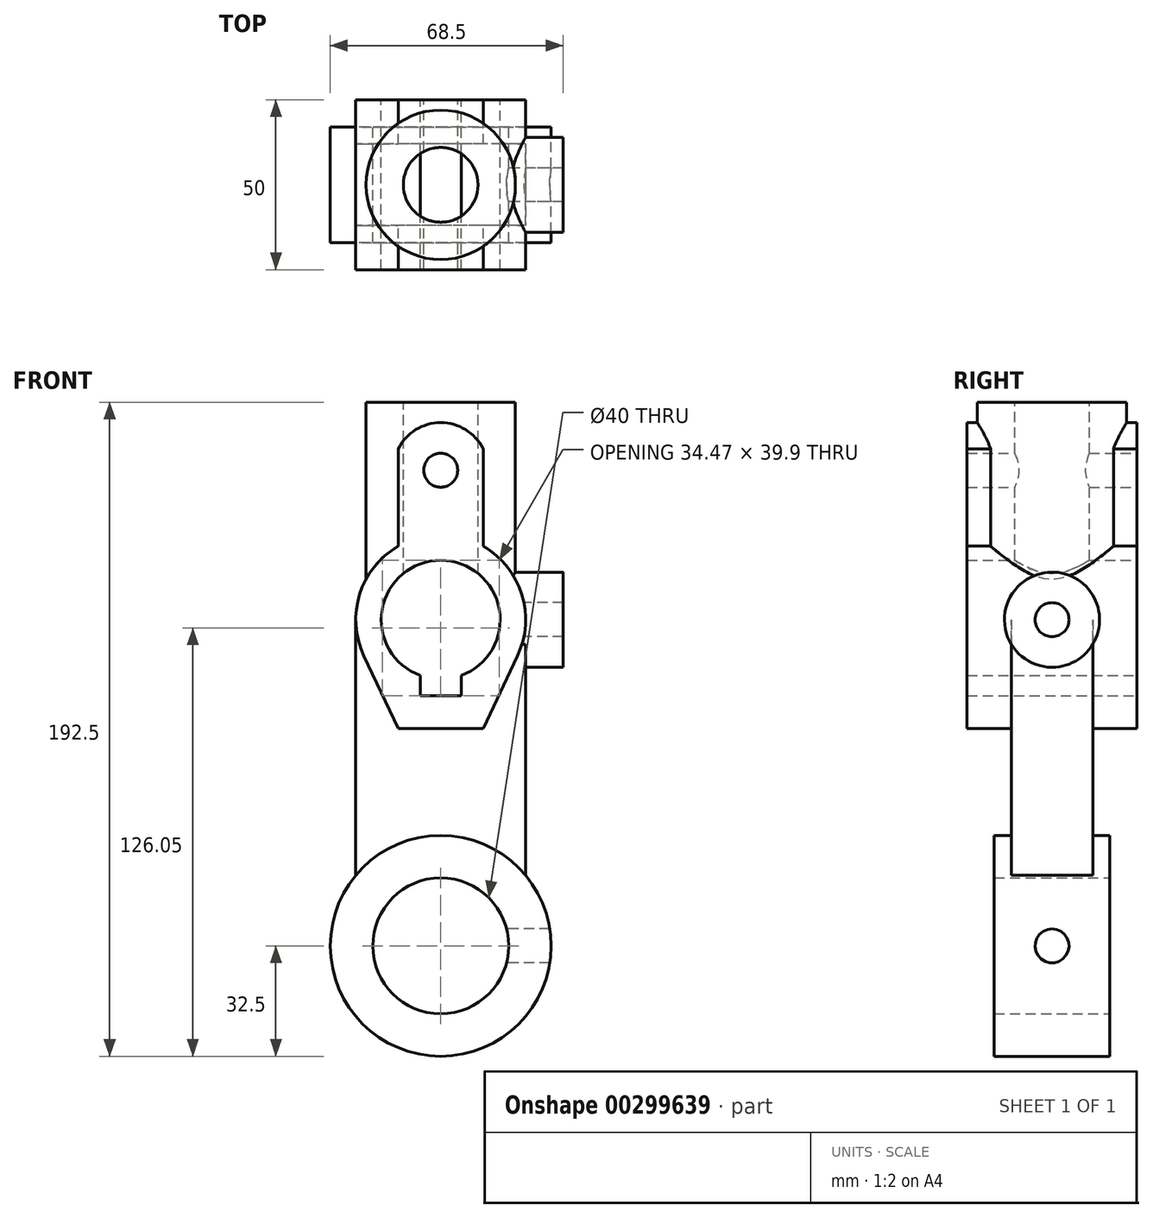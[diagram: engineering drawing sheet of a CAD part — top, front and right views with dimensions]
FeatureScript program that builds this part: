
annotation { "Feature Type Name" : "Feature", "Feature Type Description" : "" }
export const myFeature = defineFeature(function(context is Context, id is Id, definition is map)
    precondition{}
    {
        {
            var Q0;
            Q0=qCreatedBy(makeId("Front.planeOp"),FACE);
            var sketch = newSketch(context, id + "F0", { "sketchPlane" : qUnion([Q0])});
            skCircle(sketch, "E0", {"center": v(0, 0) * mm, "radius": 32.5 * mm});
            skCircle(sketch, "E1", {"center": v(0, 0) * mm, "radius": 20 * mm});
            skPoint(sketch, "E2.trimOffspring.end.orphan", {"position": v(25, 0) * mm});
            skPoint(sketch, "E3.left.start.orphan", {"position": v(-25, 0) * mm});
            skSolve(sketch);
        }
        {
            var Q0;
            Q0 = qSketchRegion(id + "F0", true);
            extrude(context, id + "F1", {"entities" : qUnion([Q0]), "endBound" : BoundingType.SYMMETRIC, "depth" : 34 * mm});
        }
        {
            var Q0;
            Q0=qCreatedBy(makeId("Front.planeOp"),FACE);
            var sketch = newSketch(context, id + "F2", { "sketchPlane" : qUnion([Q0])});
            skLineSegment(sketch, "E4", {"start": v(-25, 0) * mm, "end": v(25, 0) * mm});
            skLineSegment(sketch, "E5", {"start": v(25, 0) * mm, "end": v(25, 96) * mm});
            skLineSegment(sketch, "E6", {"start": v(-25, 0) * mm, "end": v(-25, 96) * mm});
            skLineSegment(sketch, "E7", {"start": v(-25, 96) * mm, "end": v(25, 96) * mm});
            skSolve(sketch);
        }
        {
            var Q0;
            Q0=makeQuery(id+"F2.imprint","IMPRINT",FACE,{"disambiguationData":[TD([[makeQuery(id+"F2.imprint","IMPRINT",EDGE,{"derivedFrom":sQuery(id+"F2.wireOp",EDGE,"E4")}),1.0]])]});
            extrude(context, id + "F3", {"entities" : qUnion([Q0]), "operationType" : NewBodyOperationType.ADD, "endBound" : BoundingType.SYMMETRIC, "depth" : 24 * mm});
        }
        {
            var Q0;
            {var subQ0=sQuery(id+"F2.wireOp",EDGE,"E4");Q0=makeQuery(id+"F3.boolean.opBoolean","SPLIT",FACE,{"disambiguationData":[TD([makeQuery(id+"F1.opExtrude","SWEPT_FACE",FACE,{"disambiguationData":[OSD([sQuery(id+"F0.wireOp",EDGE,"E1")])]})])],"derivedFrom":makeQuery(id+"F3.opExtrude","CAP_FACE",FACE,{"disambiguationData":[OSD([subQ0,sQuery(id+"F2.wireOp",EDGE,"E5"),sQuery(id+"F2.wireOp",EDGE,"E6"),sQuery(id+"F2.wireOp",EDGE,"E7")])],"isStart":false})});}
            extrude(context, id + "F4", {"entities" : qUnion([Q0]), "operationType" : NewBodyOperationType.REMOVE, "endBound" : BoundingType.THROUGH_ALL, "oppositeDirection" : true, "depth" : 25 * mm});
        }
        {
            var Q0;
            Q0=qCreatedBy(makeId("Front.planeOp"),FACE);
            var sketch = newSketch(context, id + "F5", { "sketchPlane" : qUnion([Q0])});
            skArc(sketch, "E8", {"start": v(6, 79.56) * mm, "mid": v(0, 113.5) * mm, "end": v(-6, 79.56) * mm});
            skLineSegment(sketch, "E9", {"start": v(-6, 79.56) * mm, "end": v(-6, 73.6) * mm});
            skLineSegment(sketch, "E10", {"start": v(6, 79.56) * mm, "end": v(6, 73.6) * mm});
            skLineSegment(sketch, "E11", {"start": v(-6, 73.6) * mm, "end": v(6, 73.6) * mm});
            skLineSegment(sketch, "E12", {"start": v(0, 78.5) * mm, "end": v(0, 73.6) * mm, "construction": true});
            skLineSegment(sketch, "E13", {"start": v(-12.5, 64) * mm, "end": v(12.5, 64) * mm});
            skLineSegment(sketch, "E14", {"start": v(12.5, 64) * mm, "end": v(22.6, 85.3) * mm});
            skLineSegment(sketch, "E15", {"start": v(-12.5, 64) * mm, "end": v(-22.6, 85.3) * mm});
            skArc(sketch, "E16", {"start": v(-22.6, 85.3) * mm, "mid": v(-23.87, 103.44) * mm, "end": v(-12.5, 117.65) * mm});
            skArc(sketch, "E17", {"start": v(22.6, 85.3) * mm, "mid": v(23.87, 103.44) * mm, "end": v(12.5, 117.65) * mm});
            skLineSegment(sketch, "E18", {"start": v(-12.5, 117.65) * mm, "end": v(-12.5, 146.3) * mm});
            skLineSegment(sketch, "E19", {"start": v(12.5, 117.65) * mm, "end": v(12.5, 146.3) * mm});
            skArc(sketch, "E20", {"start": v(12.5, 146.3) * mm, "mid": v(0, 154) * mm, "end": v(-12.5, 146.3) * mm});
            skLineSegment(sketch, "E21", {"start": v(0, 78.5) * mm, "end": v(0, 64) * mm, "construction": true});
            skCircle(sketch, "E22", {"center": v(0, 140) * mm, "radius": 5 * mm});
            skSolve(sketch);
        }
        {
            var Q0;
            Q0 = qSketchRegion(id + "F5", true);
            extrude(context, id + "F6", {"entities" : qUnion([Q0]), "operationType" : NewBodyOperationType.ADD, "endBound" : BoundingType.SYMMETRIC, "depth" : 50 * mm});
        }
        {
            var Q0;
            {var subQ0=sQuery(id+"F2.wireOp",EDGE,"E7");var subQ1=makeQuery(id+"F3.opExtrude","SWEPT_FACE",FACE,{"disambiguationData":[OSD([subQ0])]});var subQ2=sQuery(id+"F2.wireOp",EDGE,"E5");var subQ3=sQuery(id+"F2.wireOp",EDGE,"E6");Q0=makeQuery(id+"F6.boolean.opBoolean","SPLIT",FACE,{"disambiguationData":[TD([subQ1])],"derivedFrom":makeQuery(id+"F3.boolean.opBoolean","SPLIT",FACE,{"disambiguationData":[TD([makeQuery(id+"F1.opExtrude","SWEPT_FACE",FACE,{"disambiguationData":[OSD([sQuery(id+"F0.wireOp",EDGE,"E0")])]})])],"derivedFrom":makeQuery(id+"F3.opExtrude","CAP_FACE",FACE,{"disambiguationData":[OSD([sQuery(id+"F2.wireOp",EDGE,"E4"),subQ2,subQ3,subQ0])],"isStart":false})})});}
            extrude(context, id + "F7", {"entities" : qUnion([Q0]), "operationType" : NewBodyOperationType.REMOVE, "endBound" : BoundingType.THROUGH_ALL, "oppositeDirection" : true, "depth" : 25 * mm});
        }
        {
            var Q0;
            Q0=qCreatedBy(makeId("Right.planeOp"),FACE);
            var sketch = newSketch(context, id + "F8", { "sketchPlane" : qUnion([Q0])});
            skCircle(sketch, "E23", {"center": v(0, 96) * mm, "radius": 14 * mm});
            skCircle(sketch, "E24", {"center": v(0, 96) * mm, "radius": 5 * mm});
            skSolve(sketch);
        }
        {
            var Q0;
            Q0 = qSketchRegion(id + "F8", true);
            extrude(context, id + "F9", {"entities" : qUnion([Q0]), "operationType" : NewBodyOperationType.ADD, "depth" : 36 * mm});
        }
        {
            var Q0;
            Q0=qCreatedBy(makeId("Front.planeOp"),FACE);
            var sketch = newSketch(context, id + "F10", { "sketchPlane" : qUnion([Q0])});
            skCircle(sketch, "E25", {"center": v(0, 96) * mm, "radius": 17.5 * mm});
            skSolve(sketch);
        }
        {
            var Q0;
            Q0 = qSketchRegion(id + "F10", true);
            extrude(context, id + "F11", {"entities" : qUnion([Q0]), "operationType" : NewBodyOperationType.REMOVE, "endBound" : BoundingType.THROUGH_ALL, "oppositeDirection" : true, "depth" : 25 * mm, "hasSecondDirection" : true, "secondDirectionBound" : SecondDirectionBoundingType.THROUGH_ALL, "secondDirectionOppositeDirection" : false, "secondDirectionDepth" : 25 * mm});
        }
        {
            var Q0;
            Q0=qCreatedBy(makeId("Top.planeOp"),FACE);
            cPlane(context, id + "F12", {"entities" : qUnion([Q0]), "cplaneType" : CPlaneType.OFFSET, "offset" : 160 * mm, "width" : 150 * mm, "height" : 150 * mm});
        }
        {
            var Q0;
            Q0=qCreatedBy(id+"F12.planeOp",FACE);
            var sketch = newSketch(context, id + "F13", { "sketchPlane" : qUnion([Q0])});
            skCircle(sketch, "E26", {"center": v(0, 0) * mm, "radius": 22 * mm});
            skCircle(sketch, "E27", {"center": v(0, 0) * mm, "radius": 11 * mm});
            skSolve(sketch);
        }
        {
            var Q0;
            Q0 = qSketchRegion(id + "F13", true);
            extrude(context, id + "F14", {"entities" : qUnion([Q0]), "operationType" : NewBodyOperationType.ADD, "endBound" : BoundingType.UP_TO_NEXT, "oppositeDirection" : true, "depth" : 25 * mm});
        }
        {
            var Q0;
            Q0=qCreatedBy(makeId("Right.planeOp"),FACE);
            var sketch = newSketch(context, id + "F15", { "sketchPlane" : qUnion([Q0])});
            skCircle(sketch, "E28", {"center": v(0, 0) * mm, "radius": 5 * mm});
            skSolve(sketch);
        }
        {
            var Q0;
            Q0=makeQuery(id+"F13.imprint","IMPRINT",FACE,{"disambiguationData":[TD([[makeQuery(id+"F13.imprint","IMPRINT",EDGE,{"derivedFrom":sQuery(id+"F13.wireOp",EDGE,"E27")}),1.0]])]});
            extrude(context, id + "F16", {"entities" : qUnion([Q0]), "operationType" : NewBodyOperationType.REMOVE, "oppositeDirection" : true, "depth" : 56 * mm});
        }
        {
            var Q0;
            Q0 = qSketchRegion(id + "F15", true);
            extrude(context, id + "F17", {"entities" : qUnion([Q0]), "operationType" : NewBodyOperationType.REMOVE, "endBound" : BoundingType.THROUGH_ALL, "depth" : 25 * mm});
        }
    });
